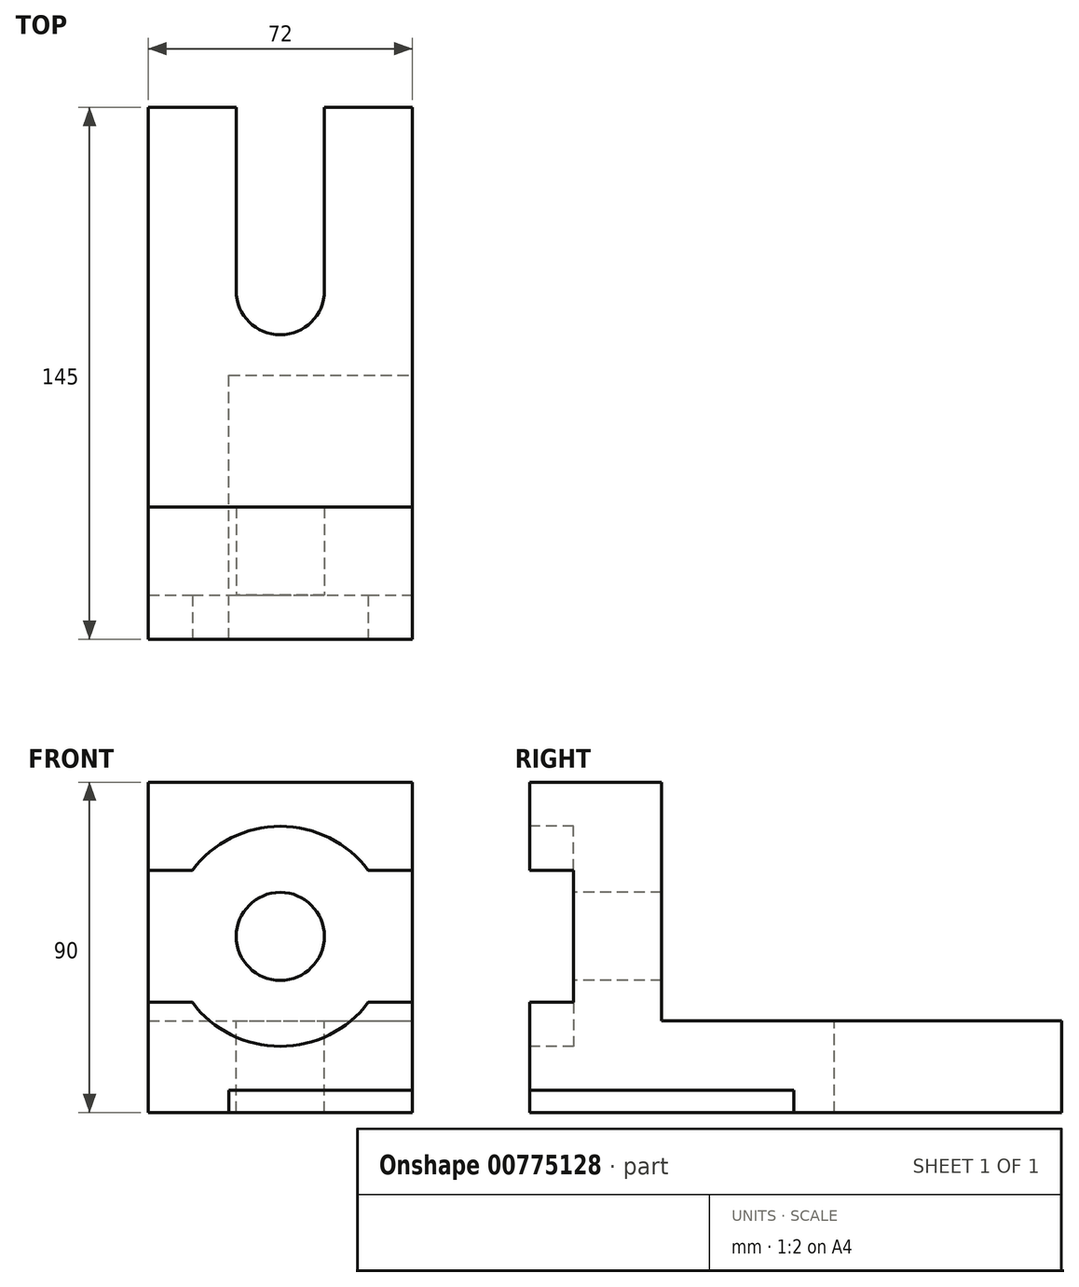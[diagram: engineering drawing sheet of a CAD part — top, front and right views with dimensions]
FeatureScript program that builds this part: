
annotation { "Feature Type Name" : "Feature", "Feature Type Description" : "" }
export const myFeature = defineFeature(function(context is Context, id is Id, definition is map)
    precondition{}
    {
        {
            var Q0;
            Q0=qCreatedBy(makeId("Top.planeOp"),FACE);
            var sketch = newSketch(context, id + "F0", { "sketchPlane" : qUnion([Q0])});
            skLineSegment(sketch, "E0.bottom", {"start": v(-31.7, -50.08) * mm, "end": v(40.3, -50.08) * mm});
            skLineSegment(sketch, "E0.top", {"start": v(-31.7, 94.92) * mm, "end": v(40.3, 94.92) * mm});
            skLineSegment(sketch, "E0.left", {"start": v(-31.7, -50.08) * mm, "end": v(-31.7, 94.92) * mm});
            skLineSegment(sketch, "E0.right", {"start": v(40.3, -50.08) * mm, "end": v(40.3, 94.92) * mm});
            skSolve(sketch);
        }
        {
            var Q0;
            Q0 = qSketchRegion(id + "F0", true);
            extrude(context, id + "F1", {"entities" : qUnion([Q0]), "depth" : 90 * mm, "offsetDistance" : 25 * mm});
        }
        {
            var Q0;
            Q0=makeQuery(id+"F1.opExtrude","SWEPT_FACE",FACE,{"disambiguationData":[OSD([sQuery(id+"F0.wireOp",EDGE,"E0.right")])]});
            var sketch = newSketch(context, id + "F2", { "sketchPlane" : qUnion([Q0])});
            skLineSegment(sketch, "E1.bottom", {"start": v(94.92, 25) * mm, "end": v(-14.08, 25) * mm});
            skLineSegment(sketch, "E1.top", {"start": v(94.92, 90) * mm, "end": v(-14.08, 90) * mm});
            skLineSegment(sketch, "E1.left", {"start": v(94.92, 25) * mm, "end": v(94.92, 90) * mm});
            skLineSegment(sketch, "E1.right", {"start": v(-14.08, 25) * mm, "end": v(-14.08, 90) * mm});
            skSolve(sketch);
        }
        {
            var Q0;
            Q0=makeQuery(id+"F2.imprint","IMPRINT",FACE,{"disambiguationData":[TD([[makeQuery(id+"F2.imprint","IMPRINT",EDGE,{"derivedFrom":sQuery(id+"F2.wireOp",EDGE,"E1.bottom")}),-1.0]])]});
            extrude(context, id + "F3", {"entities" : qUnion([Q0]), "operationType" : NewBodyOperationType.REMOVE, "oppositeDirection" : true, "depth" : 72 * mm, "offsetDistance" : 25 * mm});
        }
        {
            var Q0;
            Q0=makeQuery(id+"F1.opExtrude","CAP_FACE",FACE,{"disambiguationData":[OSD([sQuery(id+"F0.wireOp",EDGE,"E0.bottom"),sQuery(id+"F0.wireOp",EDGE,"E0.top"),sQuery(id+"F0.wireOp",EDGE,"E0.left"),sQuery(id+"F0.wireOp",EDGE,"E0.right")])],"isStart":true});
            var sketch = newSketch(context, id + "F4", { "sketchPlane" : qUnion([Q0])});
            skPoint(sketch, "E2", {"position": v(-9.7, 50.08) * mm});
            skPoint(sketch, "E3", {"position": v(40.3, -21.92) * mm});
            skLineSegment(sketch, "E4.bottom", {"start": v(-9.7, 50.08) * mm, "end": v(40.3, 50.08) * mm});
            skLineSegment(sketch, "E4.top", {"start": v(-9.7, -21.92) * mm, "end": v(40.3, -21.92) * mm});
            skLineSegment(sketch, "E4.left", {"start": v(-9.7, 50.08) * mm, "end": v(-9.7, -21.92) * mm});
            skLineSegment(sketch, "E4.right", {"start": v(40.3, 50.08) * mm, "end": v(40.3, -21.92) * mm});
            skSolve(sketch);
        }
        {
            var Q0;
            Q0=makeQuery(id+"F4.imprint","IMPRINT",FACE,{"disambiguationData":[TD([[makeQuery(id+"F4.imprint","IMPRINT",EDGE,{"derivedFrom":sQuery(id+"F4.wireOp",EDGE,"E4.bottom")}),-1.0]])]});
            extrude(context, id + "F5", {"entities" : qUnion([Q0]), "operationType" : NewBodyOperationType.REMOVE, "oppositeDirection" : true, "depth" : 6 * mm, "offsetDistance" : 25 * mm});
        }
        {
            var Q0;
            Q0=makeQuery(id+"F3.boolean.opBoolean","COPY",FACE,{"derivedFrom":makeQuery(id+"F3.opExtrude","SWEPT_FACE",FACE,{"disambiguationData":[OSD([sQuery(id+"F2.wireOp",EDGE,"E1.bottom")])]})});
            var sketch = newSketch(context, id + "F6", { "sketchPlane" : qUnion([Q0])});
            skPoint(sketch, "E5", {"position": v(-7.7, 94.92) * mm});
            skPoint(sketch, "E6", {"position": v(16.3, 94.92) * mm});
            skLineSegment(sketch, "E7.bottom", {"start": v(-7.7, 94.92) * mm, "end": v(16.3, 94.92) * mm});
            skLineSegment(sketch, "E7.left", {"start": v(-7.7, 94.92) * mm, "end": v(-7.7, 44.92) * mm});
            skLineSegment(sketch, "E7.right", {"start": v(16.3, 94.92) * mm, "end": v(16.3, 44.92) * mm});
            skArc(sketch, "E8", {"start": v(-7.7, 44.92) * mm, "mid": v(4.3, 32.92) * mm, "end": v(16.3, 44.92) * mm});
            skSolve(sketch);
        }
        {
            var Q0;
            Q0=makeQuery(id+"F6.imprint","IMPRINT",FACE,{"disambiguationData":[TD([[makeQuery(id+"F6.imprint","IMPRINT",EDGE,{"derivedFrom":sQuery(id+"F6.wireOp",EDGE,"E7.bottom")}),-1.0]])]});
            extrude(context, id + "F7", {"entities" : qUnion([Q0]), "operationType" : NewBodyOperationType.REMOVE, "oppositeDirection" : true, "depth" : 25 * mm, "offsetDistance" : 25 * mm});
        }
        {
            var Q0;
            Q0=makeQuery(id+"F1.opExtrude","SWEPT_FACE",FACE,{"disambiguationData":[OSD([sQuery(id+"F0.wireOp",EDGE,"E0.bottom")])]});
            var sketch = newSketch(context, id + "F8", { "sketchPlane" : qUnion([Q0])});
            skLineSegment(sketch, "E9.bottom", {"start": v(-31.7, 66) * mm, "end": v(-19.7, 66) * mm});
            skLineSegment(sketch, "E9.top", {"start": v(-31.7, 30) * mm, "end": v(-19.7, 30) * mm});
            skLineSegment(sketch, "E9.left", {"start": v(-31.7, 66) * mm, "end": v(-31.7, 30) * mm});
            skLineSegment(sketch, "E9.right", {"start": v(40.3, 66) * mm, "end": v(40.3, 30) * mm});
            skPoint(sketch, "E10", {"position": v(4.3, 48) * mm});
            skArc(sketch, "E11", {"start": v(28.3, 66) * mm, "mid": v(4.3, 78) * mm, "end": v(-19.7, 66) * mm});
            skLineSegment(sketch, "E12.trimOffspring", {"start": v(28.3, 66) * mm, "end": v(40.3, 66) * mm});
            skLineSegment(sketch, "E13.trimOffspring", {"start": v(28.3, 30) * mm, "end": v(40.3, 30) * mm});
            skArc(sketch, "E14.trimOffspring", {"start": v(-19.7, 30) * mm, "mid": v(4.3, 18) * mm, "end": v(28.3, 30) * mm});
            skCircle(sketch, "E15", {"center": v(4.3, 48) * mm, "radius": 12 * mm});
            skSolve(sketch);
        }
        {
            var Q0;
            Q0=makeQuery(id+"F8.imprint","IMPRINT",FACE,{"disambiguationData":[TD([[makeQuery(id+"F8.imprint","IMPRINT",EDGE,{"derivedFrom":sQuery(id+"F8.wireOp",EDGE,"E9.bottom")}),-1.0]])]});
            extrude(context, id + "F9", {"entities" : qUnion([Q0]), "operationType" : NewBodyOperationType.REMOVE, "oppositeDirection" : true, "depth" : 12 * mm, "offsetDistance" : 25 * mm});
        }
        {
            var Q0;
            Q0=makeQuery(id+"F8.imprint","IMPRINT",FACE,{"disambiguationData":[TD([[makeQuery(id+"F8.imprint","IMPRINT",EDGE,{"derivedFrom":sQuery(id+"F8.wireOp",EDGE,"E15")}),1.0]])]});
            extrude(context, id + "F10", {"entities" : qUnion([Q0]), "operationType" : NewBodyOperationType.REMOVE, "oppositeDirection" : true, "depth" : 36 * mm, "offsetDistance" : 25 * mm});
        }
    });
